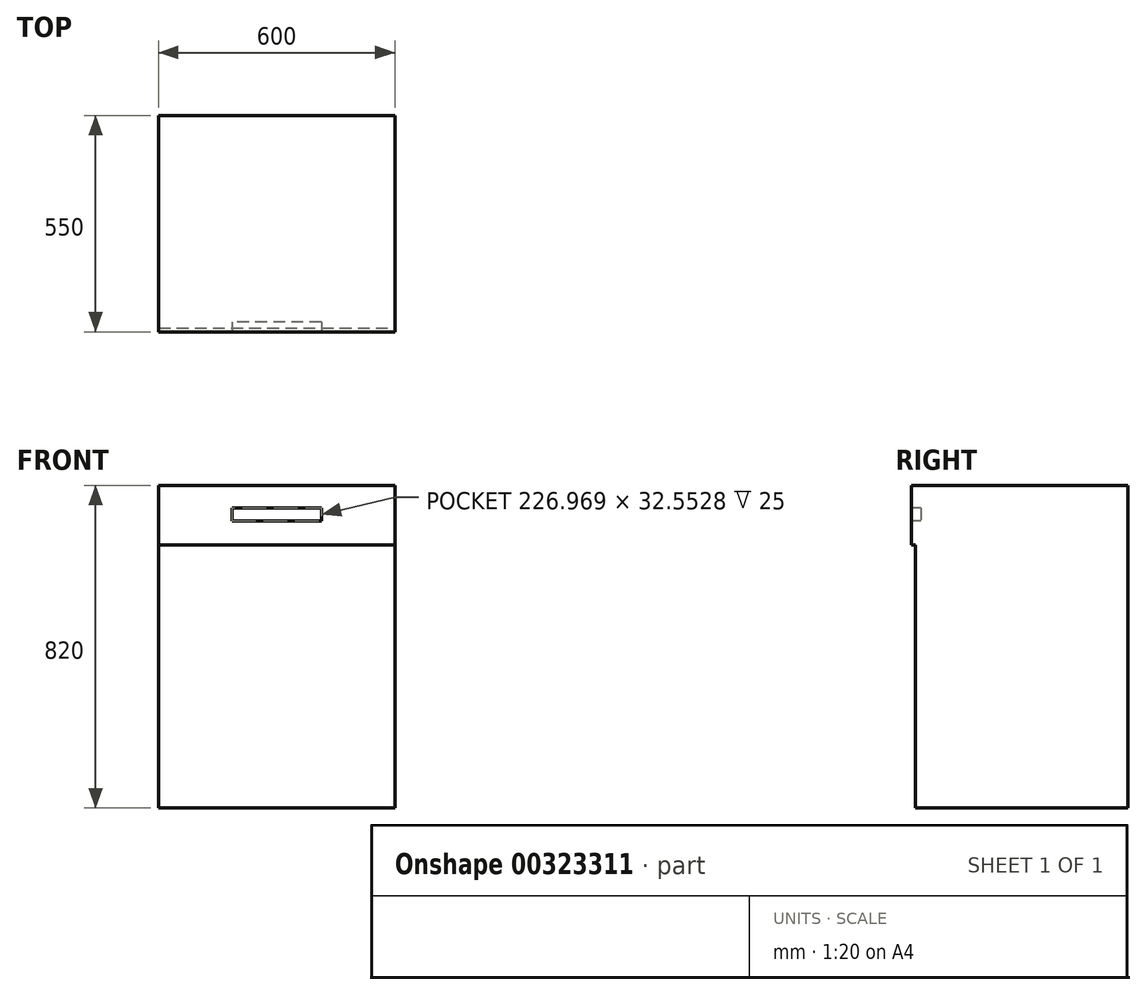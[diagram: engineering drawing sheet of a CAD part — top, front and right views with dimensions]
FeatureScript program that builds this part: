
annotation { "Feature Type Name" : "Feature", "Feature Type Description" : "" }
export const myFeature = defineFeature(function(context is Context, id is Id, definition is map)
    precondition{}
    {
        {
            var Q0;
            Q0=qCreatedBy(makeId("Front.planeOp"),FACE);
            var sketch = newSketch(context, id + "F0", { "sketchPlane" : qUnion([Q0])});
            skLineSegment(sketch, "E0.bottom", {"start": v(0, 0) * mm, "end": v(600, 0) * mm});
            skLineSegment(sketch, "E0.top", {"start": v(0, 820) * mm, "end": v(600, 820) * mm});
            skLineSegment(sketch, "E0.left", {"start": v(0, 0) * mm, "end": v(0, 820) * mm});
            skLineSegment(sketch, "E0.right", {"start": v(600, 0) * mm, "end": v(600, 820) * mm});
            skSolve(sketch);
        }
        {
            var Q0;
            Q0 = qSketchRegion(id + "F0", true);
            extrude(context, id + "F1", {"entities" : qUnion([Q0]), "depth" : 550 * mm});
        }
        {
            var Q0;
            Q0=makeQuery(id+"F1.opExtrude","CAP_FACE",FACE,{"disambiguationData":[OSD([sQuery(id+"F0.wireOp",EDGE,"E0.bottom"),sQuery(id+"F0.wireOp",EDGE,"E0.top"),sQuery(id+"F0.wireOp",EDGE,"E0.left"),sQuery(id+"F0.wireOp",EDGE,"E0.right")])],"isStart":false});
            var sketch = newSketch(context, id + "F2", { "sketchPlane" : qUnion([Q0])});
            skLineSegment(sketch, "E1", {"start": v(300, 820) * mm, "end": v(300, 0) * mm, "construction": true});
            skLineSegment(sketch, "E2.bottom", {"start": v(413.48, 762.58) * mm, "end": v(186.52, 762.58) * mm});
            skLineSegment(sketch, "E2.top", {"start": v(413.48, 730.03) * mm, "end": v(186.52, 730.03) * mm});
            skLineSegment(sketch, "E2.left", {"start": v(413.48, 762.58) * mm, "end": v(413.48, 730.03) * mm});
            skLineSegment(sketch, "E2.right", {"start": v(186.52, 762.58) * mm, "end": v(186.52, 730.03) * mm});
            skPoint(sketch, "E2.middle", {"position": v(300, 746.3) * mm});
            skSolve(sketch);
        }
        {
            var Q0;
            Q0 = qSketchRegion(id + "F2", true);
            extrude(context, id + "F3", {"entities" : qUnion([Q0]), "operationType" : NewBodyOperationType.REMOVE, "oppositeDirection" : true, "depth" : 25 * mm});
        }
        {
            var Q0;
            Q0=makeQuery(id+"F1.opExtrude","CAP_FACE",FACE,{"disambiguationData":[OSD([sQuery(id+"F0.wireOp",EDGE,"E0.bottom"),sQuery(id+"F0.wireOp",EDGE,"E0.top"),sQuery(id+"F0.wireOp",EDGE,"E0.left"),sQuery(id+"F0.wireOp",EDGE,"E0.right")])],"isStart":false});
            var sketch = newSketch(context, id + "F4", { "sketchPlane" : qUnion([Q0])});
            skLineSegment(sketch, "E3.bottom", {"start": v(0, 0) * mm, "end": v(600, 0) * mm});
            skLineSegment(sketch, "E3.top", {"start": v(0, 668.57) * mm, "end": v(600, 668.57) * mm});
            skLineSegment(sketch, "E3.left", {"start": v(0, 0) * mm, "end": v(0, 668.57) * mm});
            skLineSegment(sketch, "E3.right", {"start": v(600, 0) * mm, "end": v(600, 668.57) * mm});
            skSolve(sketch);
        }
        {
            var Q0;
            Q0 = qSketchRegion(id + "F4", true);
            extrude(context, id + "F5", {"entities" : qUnion([Q0]), "operationType" : NewBodyOperationType.REMOVE, "oppositeDirection" : true, "depth" : 10 * mm});
        }
    });
